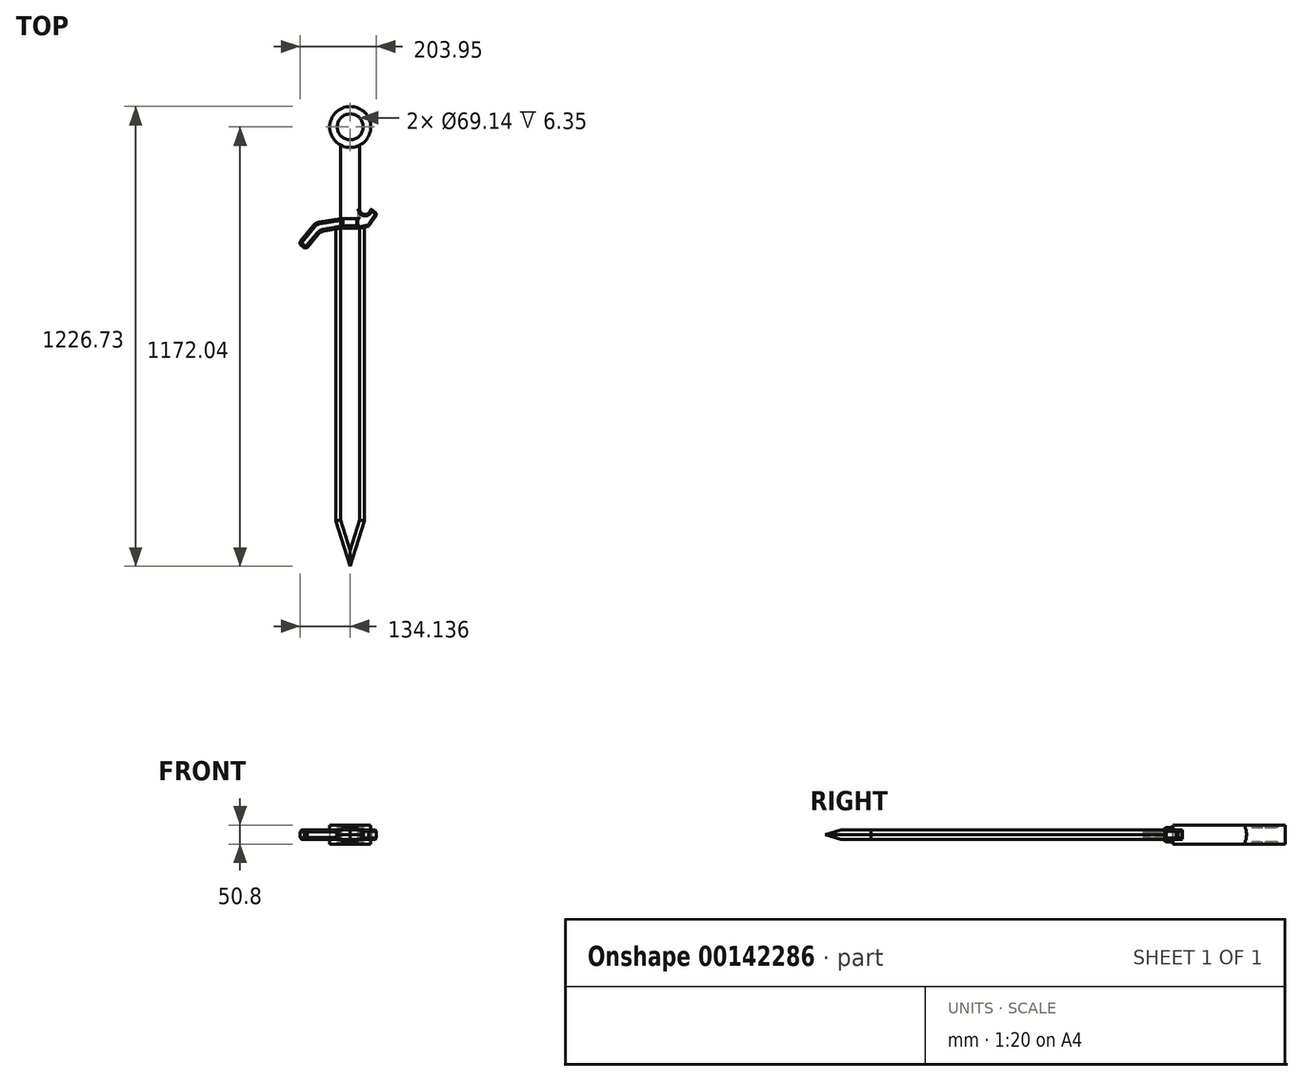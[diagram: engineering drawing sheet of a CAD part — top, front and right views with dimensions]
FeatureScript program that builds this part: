
annotation { "Feature Type Name" : "Feature", "Feature Type Description" : "" }
export const myFeature = defineFeature(function(context is Context, id is Id, definition is map)
    precondition{}
    {
        {
            var Q0;
            Q0=qCreatedBy(makeId("Top.planeOp"),FACE);
            var sketch = newSketch(context, id + "F0", { "sketchPlane" : qUnion([Q0])});
            skLineSegment(sketch, "E0", {"start": v(0, 0) * mm, "end": v(0, 203.2) * mm});
            skLineSegment(sketch, "E1", {"start": v(0, 203.2) * mm, "end": v(50.8, 203.2) * mm});
            skLineSegment(sketch, "E2", {"start": v(50.8, 203.2) * mm, "end": v(50.8, 0) * mm});
            skLineSegment(sketch, "E3", {"start": v(50.8, 0) * mm, "end": v(0, 0) * mm});
            skSolve(sketch);
        }
        {
            var Q0;
            Q0=sQuery(id+"F0.wireOp",VERTEX,"E2.start");
            var Q1;
            Q1=qCreatedBy(makeId("Front.planeOp"),FACE);
            cPlane(context, id + "F1", {"entities" : qUnion([Q0, Q1]), "cplaneType" : CPlaneType.PLANE_POINT, "offset" : 25.4 * mm, "width" : 152.4 * mm, "height" : 152.4 * mm});
        }
        {
            var Q0;
            Q0=qCreatedBy(makeId("Top.planeOp"),FACE);
            var sketch = newSketch(context, id + "F2", { "sketchPlane" : qUnion([Q0])});
            skLineSegment(sketch, "E4", {"start": v(0, 0) * mm, "end": v(-57.65, -9.47) * mm});
            skLineSegment(sketch, "E5", {"start": v(-73.1, -18.34) * mm, "end": v(-111.97, -65.3) * mm});
            skLineSegment(sketch, "E6", {"start": v(-111.97, -65.3) * mm, "end": v(-92.4, -81.5) * mm});
            skLineSegment(sketch, "E7", {"start": v(-92.4, -81.5) * mm, "end": v(-60, -42.36) * mm});
            skLineSegment(sketch, "E8", {"start": v(-44.98, -33.57) * mm, "end": v(0, -25.4) * mm});
            skLineSegment(sketch, "E9", {"start": v(0, -25.4) * mm, "end": v(0, 0) * mm});
            skLineSegment(sketch, "E10", {"start": v(0, 0) * mm, "end": v(0, 0) * mm});
            skPoint(sketch, "E11.visualSharp", {"position": v(-67.03, -11.02) * mm});
            skArc(sketch, "E11.filletArc", {"start": v(-57.65, -9.47) * mm, "mid": v(-66.17, -12.5) * mm, "end": v(-73.1, -18.34) * mm});
            skPoint(sketch, "E12.visualSharp", {"position": v(-54.1, -35.23) * mm});
            skArc(sketch, "E12.filletArc", {"start": v(-44.98, -33.57) * mm, "mid": v(-53.27, -36.64) * mm, "end": v(-60, -42.36) * mm});
            skLineSegment(sketch, "E13", {"start": v(0, 0) * mm, "end": v(45.6, 0) * mm});
            skLineSegment(sketch, "E14", {"start": v(50.8, -25.4) * mm, "end": v(0, -25.4) * mm});
            skLineSegment(sketch, "E15", {"start": v(82.97, 24.48) * mm, "end": v(97.1, 11.72) * mm});
            skLineSegment(sketch, "E16", {"start": v(97.1, 11.72) * mm, "end": v(75.55, -19.7) * mm});
            skLineSegment(sketch, "E17", {"start": v(75.55, -19.7) * mm, "end": v(50.8, -25.4) * mm});
            skLineSegment(sketch, "E18", {"start": v(50.67, 24.48) * mm, "end": v(50.67, 25.4) * mm});
            skArc(sketch, "E19", {"start": v(50.67, 25.4) * mm, "mid": v(64.46, 10.7) * mm, "end": v(79.16, 24.48) * mm});
            skLineSegment(sketch, "E20", {"start": v(79.16, 24.48) * mm, "end": v(82.97, 24.48) * mm});
            skLineSegment(sketch, "E21", {"start": v(50.67, 25.4) * mm, "end": v(45.6, 25.4) * mm});
            skLineSegment(sketch, "E22", {"start": v(45.6, 25.4) * mm, "end": v(45.6, -25.4) * mm});
            skLineSegment(sketch, "E23", {"start": v(45.6, -25.4) * mm, "end": v(50.8, -25.4) * mm});
            skPoint(sketch, "E24.orphan", {"position": v(50.67, 0) * mm});
            skSolve(sketch);
        }
        {
            var Q0;
            Q0=qCreatedBy(makeId("Top.planeOp"),FACE);
            var sketch = newSketch(context, id + "F3", { "sketchPlane" : qUnion([Q0])});
            skLineSegment(sketch, "E25", {"start": v(-12.7, -19.05) * mm, "end": v(63.5, -19.05) * mm});
            skLineSegment(sketch, "E26", {"start": v(0, 0) * mm, "end": v(25.4, 0) * mm});
            skLineSegment(sketch, "E27", {"start": v(25.4, 0) * mm, "end": v(25.4, -19.05) * mm});
            skLineSegment(sketch, "E28", {"start": v(-12.7, -19.05) * mm, "end": v(-12.7, -806.45) * mm});
            skLineSegment(sketch, "E29", {"start": v(-12.7, -806.45) * mm, "end": v(25.4, -927.6) * mm});
            skLineSegment(sketch, "E30", {"start": v(25.4, -927.6) * mm, "end": v(63.5, -806.45) * mm});
            skLineSegment(sketch, "E31", {"start": v(63.5, -806.45) * mm, "end": v(63.5, -19.05) * mm});
            skSolve(sketch);
        }
        {
            var Q0;
            Q0=makeQuery(id+"F0.imprint","IMPRINT",FACE,{"disambiguationData":[TD([[makeQuery(id+"F0.imprint","IMPRINT",EDGE,{"derivedFrom":sQuery(id+"F0.wireOp",EDGE,"E0")}),-1.0]])]});
            extrude(context, id + "F4", {"entities" : qUnion([Q0]), "endBound" : BoundingType.SYMMETRIC, "depth" : 50.8 * mm});
        }
        {
            var Q0;
            Q0=makeQuery(id+"F4.opExtrude","CAP_EDGE",EDGE,{"disambiguationData":[OSD([sQuery(id+"F0.wireOp",EDGE,"E2")])],"isStart":true});
            var Q1;
            Q1=makeQuery(id+"F4.opExtrude","CAP_EDGE",EDGE,{"disambiguationData":[OSD([sQuery(id+"F0.wireOp",EDGE,"E0")])],"isStart":true});
            var Q2;
            Q2=makeQuery(id+"F4.opExtrude","CAP_EDGE",EDGE,{"disambiguationData":[OSD([sQuery(id+"F0.wireOp",EDGE,"E0")])],"isStart":false});
            var Q3;
            Q3=makeQuery(id+"F4.opExtrude","CAP_EDGE",EDGE,{"disambiguationData":[OSD([sQuery(id+"F0.wireOp",EDGE,"E2")])],"isStart":false});
            fillet(context, id + "F5", {"entities" : qUnion([Q0, Q1, Q2, Q3]), "radius" : 25.4 * mm, "tangentPropagation" : true, "allowEdgeOverflow" : false});
        }
        {
            var Q0;
            Q0=makeQuery(id+"F2.imprint","IMPRINT",FACE,{"disambiguationData":[TD([[makeQuery(id+"F2.imprint","IMPRINT",EDGE,{"derivedFrom":sQuery(id+"F2.wireOp",EDGE,"E4")}),1.0]])]});
            var Q1;
            {var subQ4=sQuery(id+"F2.wireOp",EDGE,"xWFaYJGu-WusR-n155-9BUO-TZLnq1k2AYxH");Q1=makeQuery(id+"F2.imprint","IMPRINT",FACE,{"disambiguationData":[TD([[makeQuery(id+"F2.imprint","IMPRINT",EDGE,{"derivedFrom":subQ4}),1.0]])]});}
            var Q2;
            Q2=makeQuery(id+"F2.imprint","IMPRINT",FACE,{"disambiguationData":[TD([[makeQuery(id+"F2.imprint","IMPRINT",EDGE,{"derivedFrom":sQuery(id+"F2.wireOp",EDGE,"E15")}),-1.0]])]});
            extrude(context, id + "F6", {"entities" : qUnion([Q0, Q1, Q2]), "endBound" : BoundingType.SYMMETRIC, "depth" : 25.4 * mm});
        }
        {
            var Q0;
            Q0=makeQuery(id+"F2.imprint","IMPRINT",FACE,{"disambiguationData":[TD([[makeQuery(id+"F2.imprint","IMPRINT",EDGE,{"derivedFrom":sQuery(id+"F2.wireOp",EDGE,"E9")}),-1.0]])]});
            extrude(context, id + "F7", {"entities" : qUnion([Q0]), "endBound" : BoundingType.SYMMETRIC, "depth" : 38.1 * mm});
        }
        {
            var Q0;
            {var subQ3=sQuery(id+"F3.wireOp",EDGE,"E28");Q0=makeQuery(id+"F3.imprint","IMPRINT",FACE,{"disambiguationData":[TD([[makeQuery(id+"F3.imprint","IMPRINT",EDGE,{"derivedFrom":subQ3}),1.0]])]});}
            extrude(context, id + "F8", {"entities" : qUnion([Q0]), "endBound" : BoundingType.SYMMETRIC, "depth" : 25.4 * mm});
        }
        {
            var Q0;
            Q0=makeQuery(id+"F8.opExtrude","CAP_EDGE",EDGE,{"disambiguationData":[OSD([sQuery(id+"F3.wireOp",EDGE,"E31")])],"isStart":false});
            var Q1;
            Q1=makeQuery(id+"F8.opExtrude","CAP_EDGE",EDGE,{"disambiguationData":[OSD([sQuery(id+"F3.wireOp",EDGE,"E28")])],"isStart":true});
            var Q2;
            Q2=makeQuery(id+"F8.opExtrude","CAP_EDGE",EDGE,{"disambiguationData":[OSD([sQuery(id+"F3.wireOp",EDGE,"E28")])],"isStart":false});
            var Q3;
            Q3=makeQuery(id+"F8.opExtrude","CAP_EDGE",EDGE,{"disambiguationData":[OSD([sQuery(id+"F3.wireOp",EDGE,"E31")])],"isStart":true});
            var Q4;
            Q4=makeQuery(id+"F8.opExtrude","CAP_EDGE",EDGE,{"disambiguationData":[OSD([sQuery(id+"F3.wireOp",EDGE,"E29")])],"isStart":false});
            var Q5;
            Q5=makeQuery(id+"F8.opExtrude","CAP_EDGE",EDGE,{"disambiguationData":[OSD([sQuery(id+"F3.wireOp",EDGE,"E30")])],"isStart":false});
            var Q6;
            Q6=makeQuery(id+"F8.opExtrude","CAP_EDGE",EDGE,{"disambiguationData":[OSD([sQuery(id+"F3.wireOp",EDGE,"E30")])],"isStart":true});
            var Q7;
            Q7=makeQuery(id+"F8.opExtrude","CAP_EDGE",EDGE,{"disambiguationData":[OSD([sQuery(id+"F3.wireOp",EDGE,"E29")])],"isStart":true});
            chamfer(context, id + "F9", {"entities" : qUnion([Q0, Q1, Q2, Q3, Q4, Q5, Q6, Q7]), "width" : 12.7 * mm, "tangentPropagation" : true});
        }
        {
            var Q0;
            Q0=makeQuery(id+"F7.opExtrude","CAP_EDGE",EDGE,{"disambiguationData":[OSD([sQuery(id+"F2.wireOp",EDGE,"E9")])],"isStart":true});
            var Q1;
            Q1=makeQuery(id+"F7.opExtrude","CAP_EDGE",EDGE,{"disambiguationData":[OSD([sQuery(id+"F2.wireOp",EDGE,"E9")])],"isStart":false});
            var Q2;
            Q2=makeQuery(id+"F7.opExtrude","CAP_EDGE",EDGE,{"disambiguationData":[OSD([sQuery(id+"F2.wireOp",EDGE,"E14")])],"isStart":true});
            var Q3;
            Q3=makeQuery(id+"F7.opExtrude","CAP_EDGE",EDGE,{"disambiguationData":[OSD([sQuery(id+"F2.wireOp",EDGE,"E14")])],"isStart":false});
            chamfer(context, id + "F10", {"entities" : qUnion([Q0, Q1, Q2, Q3]), "width" : 6.35 * mm, "tangentPropagation" : true});
        }
        {
            var Q0;
            Q0=makeQuery(id+"F6.opExtrude","CAP_EDGE",EDGE,{"disambiguationData":[OSD([sQuery(id+"F2.wireOp",EDGE,"E19")])],"isStart":false});
            var Q1;
            Q1=makeQuery(id+"F6.opExtrude","SWEPT_EDGE",EDGE,{"disambiguationData":[OSD([sQuery(id+"F2.wireOp",EDGE,"E18"),sQuery(id+"F2.wireOp",EDGE,"E19"),sQuery(id+"F2.wireOp",EDGE,"E21")])]});
            var Q2;
            Q2=makeQuery(id+"F6.opExtrude","CAP_EDGE",EDGE,{"disambiguationData":[OSD([sQuery(id+"F2.wireOp",EDGE,"E19")])],"isStart":true});
            var Q3;
            Q3=makeQuery(id+"F6.opExtrude","SWEPT_EDGE",EDGE,{"disambiguationData":[OSD([sQuery(id+"F2.wireOp",EDGE,"E15"),sQuery(id+"F2.wireOp",EDGE,"E20")])]});
            var Q4;
            Q4=makeQuery(id+"F6.opExtrude","SWEPT_EDGE",EDGE,{"disambiguationData":[OSD([sQuery(id+"F2.wireOp",EDGE,"E15"),sQuery(id+"F2.wireOp",EDGE,"E16")])]});
            var Q5;
            Q5=makeQuery(id+"F6.opExtrude","SWEPT_EDGE",EDGE,{"disambiguationData":[OSD([sQuery(id+"F2.wireOp",EDGE,"E16"),sQuery(id+"F2.wireOp",EDGE,"E17")])]});
            var Q6;
            Q6=makeQuery(id+"F6.opExtrude","CAP_EDGE",EDGE,{"disambiguationData":[OSD([sQuery(id+"F2.wireOp",EDGE,"E15")])],"isStart":false});
            var Q7;
            Q7=makeQuery(id+"F6.opExtrude","CAP_EDGE",EDGE,{"disambiguationData":[OSD([sQuery(id+"F2.wireOp",EDGE,"E16")])],"isStart":false});
            var Q8;
            Q8=makeQuery(id+"F6.opExtrude","CAP_EDGE",EDGE,{"disambiguationData":[OSD([sQuery(id+"F2.wireOp",EDGE,"E15")])],"isStart":true});
            var Q9;
            Q9=makeQuery(id+"F6.opExtrude","CAP_EDGE",EDGE,{"disambiguationData":[OSD([sQuery(id+"F2.wireOp",EDGE,"E16")])],"isStart":true});
            var Q10;
            Q10=makeQuery(id+"F6.opExtrude","CAP_EDGE",EDGE,{"disambiguationData":[OSD([sQuery(id+"F2.wireOp",EDGE,"E17")])],"isStart":false});
            var Q11;
            Q11=makeQuery(id+"F6.opExtrude","CAP_EDGE",EDGE,{"disambiguationData":[OSD([sQuery(id+"F2.wireOp",EDGE,"E17")])],"isStart":true});
            chamfer(context, id + "F11", {"entities" : qUnion([Q0, Q1, Q2, Q3, Q4, Q5, Q6, Q7, Q8, Q9, Q10, Q11]), "width" : 3.8 * mm, "tangentPropagation" : true});
        }
        {
            var Q0;
            Q0=makeQuery(id+"F7.opExtrude","CAP_EDGE",EDGE,{"disambiguationData":[OSD([sQuery(id+"F2.wireOp",EDGE,"E22")])],"isStart":true});
            var Q1;
            Q1=makeQuery(id+"F7.opExtrude","CAP_EDGE",EDGE,{"disambiguationData":[OSD([sQuery(id+"F2.wireOp",EDGE,"E22")])],"isStart":false});
            chamfer(context, id + "F12", {"entities" : qUnion([Q0, Q1]), "width" : 2.54 * mm, "tangentPropagation" : true});
        }
        {
            var Q0;
            Q0=makeQuery(id+"F6.opExtrude","CAP_EDGE",EDGE,{"disambiguationData":[OSD([sQuery(id+"F2.wireOp",EDGE,"E4")])],"isStart":false});
            var Q1;
            Q1=makeQuery(id+"F6.opExtrude","CAP_EDGE",EDGE,{"disambiguationData":[OSD([sQuery(id+"F2.wireOp",EDGE,"E4")])],"isStart":true});
            var Q2;
            Q2=makeQuery(id+"F6.opExtrude","CAP_EDGE",EDGE,{"disambiguationData":[OSD([sQuery(id+"F2.wireOp",EDGE,"E8")])],"isStart":true});
            var Q3;
            Q3=makeQuery(id+"F6.opExtrude","CAP_EDGE",EDGE,{"disambiguationData":[OSD([sQuery(id+"F2.wireOp",EDGE,"E7")])],"isStart":false});
            var Q4;
            Q4=makeQuery(id+"F6.opExtrude","CAP_EDGE",EDGE,{"disambiguationData":[OSD([sQuery(id+"F2.wireOp",EDGE,"E6")])],"isStart":false});
            var Q5;
            Q5=makeQuery(id+"F6.opExtrude","SWEPT_EDGE",EDGE,{"disambiguationData":[OSD([sQuery(id+"F2.wireOp",EDGE,"E6"),sQuery(id+"F2.wireOp",EDGE,"E7")])]});
            var Q6;
            Q6=makeQuery(id+"F6.opExtrude","CAP_EDGE",EDGE,{"disambiguationData":[OSD([sQuery(id+"F2.wireOp",EDGE,"E6")])],"isStart":true});
            var Q7;
            Q7=makeQuery(id+"F6.opExtrude","SWEPT_EDGE",EDGE,{"disambiguationData":[OSD([sQuery(id+"F2.wireOp",EDGE,"E5"),sQuery(id+"F2.wireOp",EDGE,"E6")])]});
            chamfer(context, id + "F13", {"entities" : qUnion([Q0, Q1, Q2, Q3, Q4, Q5, Q6, Q7]), "width" : 5.08 * mm, "tangentPropagation" : true});
        }
        {
            var Q0;
            Q0=qCreatedBy(makeId("Top.planeOp"),FACE);
            var sketch = newSketch(context, id + "F14", { "sketchPlane" : qUnion([Q0])});
            skCircle(sketch, "E32", {"center": v(25.4, 244.44) * mm, "radius": 54.7 * mm});
            skCircle(sketch, "E33", {"center": v(25.4, 244.44) * mm, "radius": 34.57 * mm});
            skSolve(sketch);
        }
        {
            var Q0;
            Q0=makeQuery(id+"F14.imprint","IMPRINT",FACE,{"disambiguationData":[TD([[makeQuery(id+"F14.imprint","IMPRINT",EDGE,{"derivedFrom":sQuery(id+"F14.wireOp",EDGE,"E32")}),1.0]])]});
            extrude(context, id + "F15", {"entities" : qUnion([Q0]), "operationType" : NewBodyOperationType.ADD, "endBound" : BoundingType.SYMMETRIC, "depth" : 50.8 * mm});
        }
        {
            var Q0;
            Q0=makeQuery(id+"F14.imprint","IMPRINT",FACE,{"disambiguationData":[TD([[makeQuery(id+"F14.imprint","IMPRINT",EDGE,{"derivedFrom":sQuery(id+"F14.wireOp",EDGE,"E33")}),1.0]])]});
            extrude(context, id + "F16", {"entities" : qUnion([Q0]), "operationType" : NewBodyOperationType.ADD, "endBound" : BoundingType.SYMMETRIC, "depth" : 38.1 * mm});
        }
    });
